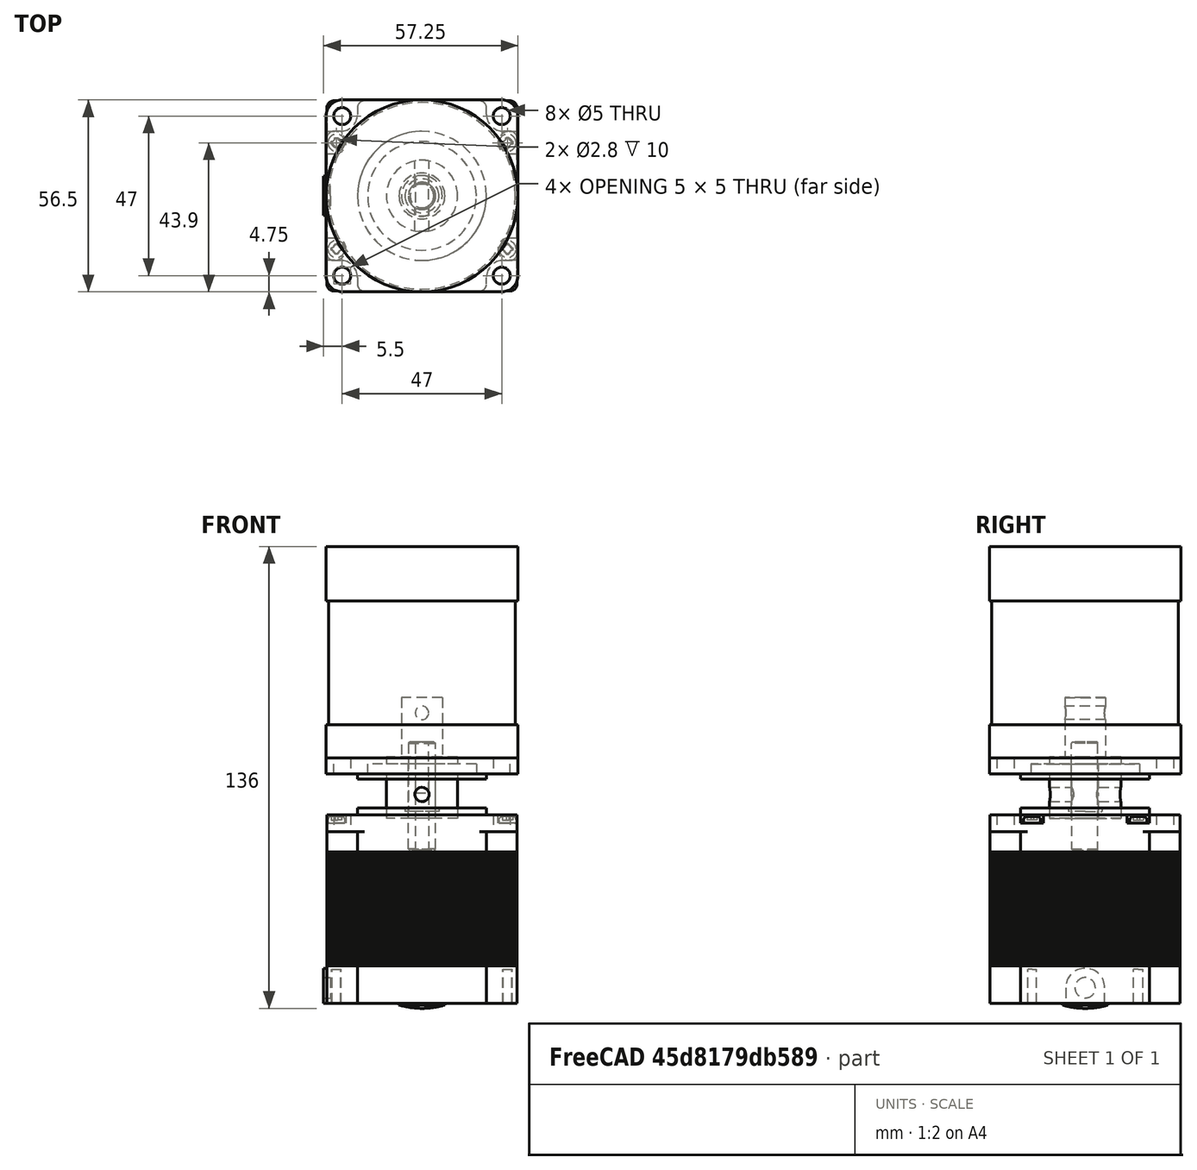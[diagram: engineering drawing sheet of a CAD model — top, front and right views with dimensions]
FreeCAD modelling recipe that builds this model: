
FCSTD DOCUMENT  (FreeCAD 0.20R29410 (Git))
Label: 57BLY-0730NBB
License: All rights reserved
LicenseURL: http://en.wikipedia.org/wiki/All_rights_reserved
objects: TechDraw::DrawViewDimension×11, PartDesign::CoordinateSystem×10, Sketcher::SketchObject×9, TechDraw::DrawProjGroupItem×4, PartDesign::Mirrored×3, PartDesign::Body×3, App::DocumentObjectGroup×3, PartDesign::Pad×2, PartDesign::Revolution×2, App::Link×2, App::Part×2, PartDesign::MultiTransform×1, PartDesign::Groove×1, PartDesign::Hole×1, Part::Feature×1, TechDraw::DrawSVGTemplate×1, App::FeaturePython×1, PartDesign::Pocket×1, TechDraw::DrawProjGroup×1, TechDraw::DrawViewSection×1, +1 more types
note: 41 computed .brp shape members not serialized (recipe doc carries the construction recipe); baked Part::Feature solids carry a one-line shape summary decoded from their .brp

FEATURE [Sketcher::SketchObject] Sketch
  FullyConstrained = true
  MapMode = 5
  Support = -> [XY_Plane]
  sketch-geometry (9):
    g0: LineSegment StartX=0 StartY=0 StartZ=0 EndX=28.25 EndY=0 EndZ=0
    g1: LineSegment StartX=28.25 StartY=0 StartZ=0 EndX=28.25 EndY=23.5386 EndZ=0
    g2: LineSegment StartX=23.5386 StartY=28.25 StartZ=0 EndX=0 EndY=28.25 EndZ=0
    g3: LineSegment StartX=0 StartY=28.25 StartZ=0 EndX=0 EndY=0 EndZ=0
    g4: ArcOfCircle CenterX=23.5386 CenterY=23.5386 CenterZ=0 NormalX=0 NormalY=0 NormalZ=1 AngleXU=0 Radius=4.71142 StartAngle=0 EndAngle=1.5708
    g5: GeomPoint X=28.25 Y=28.25 Z=0
    g6: Circle CenterX=23.5 CenterY=23.5 CenterZ=0 NormalX=0 NormalY=0 NormalZ=1 AngleXU=0 Radius=2.5
    g7: LineSegment StartX=0 StartY=0 StartZ=0 EndX=28.25 EndY=28.25 EndZ=0
    g8: GeomPoint X=26.8701 Y=26.8701 Z=0
  constraints (22):
    c: Coincident(g0,g1)
    c: Coincident(g2,g3)
    c: Coincident(g3,g0)
    c: Horizontal(g0)
    c: Horizontal(g2)
    c: Vertical(g1)
    c: Vertical(g3)
    c: Coincident(g0,g-1)
    c: Equal(g0,g3)
    c: PointOnObject(g5,g2)
    c: PointOnObject(g5,g1)
    c: Tangent(g2,g4) = -1.5708
    c: Tangent(g1,g4) = -1.5708
    c: Coincident(g7,g0)
    c: Coincident(g7,g5)
    c: PointOnObject(g6,g7)
    c: DistanceX(g6) = 23.5
    c: PointOnObject(g8,g4)
    c: PointOnObject(g8,g7)
    c: Distance(g0,g8) = 38
    c: DistanceX(g0) = 28.25  'width'
    c: Diameter(g6) = 5
FEATURE [PartDesign::Pad] Pad
  Direction = (0,0,1)
  Length = 4.7
  Length2 = 10
  Profile = -> Sketch
  ReferenceAxis = -> Sketch [N_Axis]
  Type = 0
FEATURE [PartDesign::Mirrored] Mirrored
  MirrorPlane = -> Sketch [V_Axis]
FEATURE [PartDesign::Mirrored] Mirrored001
  MirrorPlane = -> Sketch [H_Axis]
FEATURE [PartDesign::MultiTransform] MultiTransform
  BaseFeature = -> Pad
  Originals = -> [Pad]
  Transformations = -> [Mirrored,Mirrored001]
FEATURE [Sketcher::SketchObject] Sketch001
  FullyConstrained = true
  MapMode = 5
  Placement = pos=(0,0,0) rot=(1,0,0;1.5708rad)
  Support = -> [XZ_Plane]
  sketch-geometry (10):
    g0: LineSegment StartX=19 StartY=0 StartZ=0 EndX=28.25 EndY=0 EndZ=0
    g1: LineSegment StartX=28.25 StartY=0 StartZ=0 EndX=28.25 EndY=14.5 EndZ=0
    g2: LineSegment StartX=28.25 StartY=14.5 StartZ=0 EndX=27.5 EndY=14.5 EndZ=0
    g3: LineSegment StartX=27.5 StartY=14.5 StartZ=0 EndX=27.5 EndY=51 EndZ=0
    g4: LineSegment StartX=27.5 StartY=51 StartZ=0 EndX=28.25 EndY=51 EndZ=0
    g5: LineSegment StartX=28.25 StartY=51 StartZ=0 EndX=28.25 EndY=67 EndZ=0
    g6: LineSegment StartX=28.25 StartY=67 StartZ=0 EndX=0 EndY=67 EndZ=0
    g7: LineSegment StartX=0 StartY=67 StartZ=0 EndX=0 EndY=-1.5 EndZ=0
    g8: LineSegment StartX=19 StartY=0 StartZ=0 EndX=19 EndY=-1.5 EndZ=0
    g9: LineSegment StartX=19 StartY=-1.5 StartZ=0 EndX=0 EndY=-1.5 EndZ=0
  constraints (31):
    c: PointOnObject(g0,g-1)
    c: Coincident(g0,g1)
    c: Vertical(g1)
    c: Coincident(g1,g2)
    c: Horizontal(g2)
    c: Coincident(g2,g3)
    c: Vertical(g3)
    c: Coincident(g3,g4)
    c: Horizontal(g4)
    c: Coincident(g4,g5)
    c: Vertical(g5)
    c: Coincident(g5,g6)
    c: PointOnObject(g6,g-2)
    c: Horizontal(g6)
    c: Coincident(g6,g7)
    c: Distance(g1) = 14.5
    c: DistanceX(g2) = 27.5
    c: Distance(g3) = 36.5
    c: Vertical(g4,g1)
    c: Distance(g5) = 16
    c: Distance(g7) = 68.5  'total_height'
    c: Vertical(g8)
    c: Coincident(g9,g8)
    c: Horizontal(g9)
    c: DistanceX(g0) = 28.25
    c: Coincident(g0,g8)
    c: Distance(g9) = 19
    c: PointOnObject(g9,g-2)
    c: Coincident(g7,g9)
    c: DistanceY(g7,g-1) = 1.5  'bearing_height'
    c: Horizontal(g0)
FEATURE [PartDesign::Revolution] Revolution
  Angle = 360
  Axis = (0,-2e-16,1)
  Base = (0,0,0)
  BaseFeature = -> MultiTransform
  Profile = -> Sketch001
  ReferenceAxis = -> Sketch001 [V_Axis]
  Reversed = true
FEATURE [PartDesign::Body] Body
  Group = -> [Sketch,Pad,MultiTransform,Mirrored,Mirrored001,Sketch001,Revolution]
  Origin = -> Origin
  Tip = -> Revolution
FEATURE [Sketcher::SketchObject] Sketch002
  FullyConstrained = true
  MapMode = 5
  Support = -> [XY_Plane002]
  expr: .AttachmentOffset.Base.z = 0
  sketch-geometry (3):
    g0: LineSegment StartX=0 StartY=3.5 StartZ=0 EndX=1.93649 EndY=3.5 EndZ=0
    g1: ArcOfCircle CenterX=0 CenterY=0 CenterZ=0 NormalX=0 NormalY=0 NormalZ=1 AngleXU=0 Radius=4 StartAngle=4.71239 EndAngle=7.34862
    g2: LineSegment StartX=-7e-16 StartY=-4 StartZ=0 EndX=0 EndY=3.5 EndZ=0
  constraints (9):
    c: PointOnObject(g0,g-2)
    c: Horizontal(g0)
    c: Coincident(g1,g-1)
    c: PointOnObject(g1,g-2)
    c: Coincident(g1,g0)
    c: Coincident(g2,g1)
    c: Coincident(g2,g0)
    c: Distance(g2) = 7.5
    c: Diameter(g1) = 8
FEATURE [PartDesign::Pad] Pad001
  Direction = (0,0,1)
  Length = 21
  Length2 = 10
  Profile = -> Sketch002
  ReferenceAxis = -> Sketch002 [N_Axis]
  Reversed = true
  Type = 0
FEATURE [PartDesign::Mirrored] Mirrored002
  BaseFeature = -> Pad001
  MirrorPlane = -> Sketch002 [V_Axis]
  Originals = -> [Pad001]
FEATURE [Sketcher::SketchObject] Sketch003
  FullyConstrained = true
  MapMode = 5
  Placement = pos=(0,0,0) rot=(0.57735,0.57735,0.57735;2.0944rad)
  Support = -> [YZ_Plane002]
  expr: Constraints[8] = -Pad001.Length
  sketch-geometry (3):
    g0: LineSegment StartX=3.5 StartY=-21 StartZ=0 EndX=4 EndY=-20.5 EndZ=0
    g1: LineSegment StartX=4 StartY=-20.5 StartZ=0 EndX=4 EndY=-21 EndZ=0
    g2: LineSegment StartX=4 StartY=-21 StartZ=0 EndX=3.5 EndY=-21 EndZ=0
  constraints (9):
    c: Coincident(g0,g1)
    c: Vertical(g1)
    c: Coincident(g1,g2)
    c: Coincident(g2,g0)
    c: Horizontal(g2)
    c: DistanceX(g0) = 3.5
    c: DistanceX(g0) = 4
    c: Equal(g2,g1)
    c: DistanceY(g1) = -21
FEATURE [PartDesign::Groove] Groove
  Angle = 360
  Axis = (-2e-16,3e-16,1)
  Base = (0,0,0)
  BaseFeature = -> Mirrored002
  Profile = -> Sketch003
  ReferenceAxis = -> Sketch003 [V_Axis]
FEATURE [PartDesign::Body] Body001  label="axis"
  Group = -> [Sketch002,Pad001,Mirrored002,Sketch003,Groove]
  Origin = -> Origin002
  Placement = pos=(0,0,-1.5) rot=(0,0,1;0rad)
  Tip = -> Groove
  expr: .Placement.Base.z = -Sketch001.Constraints.bearing_height
FEATURE [PartDesign::CoordinateSystem] fix_center
  AttacherType = Attacher::AttachEngine3D
  MapMode = 2
  Support = -> [XY_Plane001]
FEATURE [PartDesign::CoordinateSystem] LCS_0  label="end"
  AttacherType = Attacher::AttachEngine3D
  AttachmentOffset = pos=(0,0,-13) rot=(0.707107,-0.707107,0;3.14159rad)
  MapMode = 5
  Placement = pos=(0,0,-13) rot=(0.707107,-0.707107,0;3.14159rad)
  Support = -> [XY_Plane003]
  expr: .AttachmentOffset.Base.z = -Sketch005.Constraints.axis_fuxture_cyl_length
FEATURE [Sketcher::SketchObject] Sketch005
  FullyConstrained = true
  MapMode = 5
  Placement = pos=(0,0,0) rot=(1,0,0;1.5708rad)
  Support = -> [XZ_Plane003]
  sketch-geometry (12):
    g0: LineSegment StartX=0 StartY=22.5 StartZ=0 EndX=6 EndY=22.5 EndZ=0
    g1: LineSegment StartX=6 StartY=22.5 StartZ=0 EndX=6 EndY=5 EndZ=0
    g2: LineSegment StartX=6 StartY=5 StartZ=0 EndX=10.5 EndY=5 EndZ=0
    g3: LineSegment StartX=10.5 StartY=5 StartZ=0 EndX=10.5 EndY=3 EndZ=0
    g4: LineSegment StartX=10.5 StartY=3 StartZ=0 EndX=16 EndY=3 EndZ=0
    g5: LineSegment StartX=16 StartY=3 StartZ=0 EndX=16 EndY=0 EndZ=0
    g6: LineSegment StartX=16 StartY=0 StartZ=0 EndX=10.5 EndY=0 EndZ=0
    g7: LineSegment StartX=10.5 StartY=0 StartZ=0 EndX=10.5 EndY=-13 EndZ=0
    g8: LineSegment StartX=10.5 StartY=-13 StartZ=0 EndX=4 EndY=-13 EndZ=0
    g9: LineSegment StartX=4 StartY=-13 StartZ=0 EndX=4 EndY=3 EndZ=0
    g10: LineSegment StartX=4 StartY=3 StartZ=0 EndX=0 EndY=3 EndZ=0
    g11: LineSegment StartX=0 StartY=3 StartZ=0 EndX=0 EndY=22.5 EndZ=0
  constraints (37):
    c: Horizontal(g0)
    c: Coincident(g0,g1)
    c: Vertical(g1)
    c: Coincident(g1,g2)
    c: Horizontal(g2)
    c: Coincident(g2,g3)
    c: Vertical(g3)
    c: Coincident(g3,g4)
    c: Coincident(g4,g5)
    c: Vertical(g5)
    c: Coincident(g5,g6)
    c: Horizontal(g6)
    c: Coincident(g6,g7)
    c: Vertical(g7)
    c: Coincident(g7,g8)
    c: Horizontal(g8)
    c: Coincident(g8,g9)
    c: Vertical(g9)
    c: Horizontal(g4)
    c: DistanceX(g0) = 6
    c: DistanceX(g2) = 10.5
    c: DistanceX(g4) = 16
    c: DistanceX(g7) = 10.5
    c: DistanceX(g8) = 4
    c: DistanceY(g3,g3) = 2
    c: DistanceY(g3,g0) = 19.5
    c: DistanceY(g5,g5) = 3  'shield_length'
    c: Distance(g7,g6) = 13  'axis_fuxture_cyl_length'
    c: Horizontal(g-1,g6)
    c: DistanceY(g0) = 22.5  'shield_to_end'
    c: PointOnObject(g10,g-2)
    c: Horizontal(g10)
    c: Coincident(g11,g10)
    c: Vertical(g11)
    c: DistanceY(g8,g10) = 16  'axis_length'
    c: Coincident(g9,g10)
    c: Coincident(g11,g0)
FEATURE [PartDesign::Revolution] Revolution001
  Angle = 360
  Axis = (0,-2e-16,1)
  Base = (0,0,0)
  Placement = pos=(0,0,0) rot=(1,0,0;1.5708rad)
  Profile = -> Sketch005
  ReferenceAxis = -> Sketch005 [V_Axis]
  Reversed = true
FEATURE [Sketcher::SketchObject] Sketch006
  AttachmentOffset = pos=(0,-6,20) rot=(0,0,1;0rad)
  FullyConstrained = true
  MapMode = 5
  Placement = pos=(0,-20,-6) rot=(1,0,0;1.5708rad)
  Support = -> [XZ_Plane003]
  expr: .AttachmentOffset.Base.y = -Sketch005.Constraints.axis_fuxture_cyl_length + 7mm
  sketch-geometry (1):
    g0: Circle CenterX=0 CenterY=0 CenterZ=0 NormalX=0 NormalY=0 NormalZ=1 AngleXU=0 Radius=2
  constraints (2):
    c: Coincident(g0,g-1)
    c: Diameter(g0) = 4
FEATURE [PartDesign::Hole] Hole
  BaseFeature = -> Revolution001
  CustomThreadClearance = 0
  Depth = 117.943
  DepthType = 1
  Diameter = 4.2
  DrillForDepth = false
  DrillPoint = 1
  DrillPointAngle = 117
  HoleCutCountersinkAngle = 90
  HoleCutCustomValues = false
  HoleCutDepth = 0
  HoleCutDiameter = 6.1
  HoleCutType = 0
  ModelThread = false
  Placement = pos=(0,0,0) rot=(1,0,0;1.5708rad)
  Profile = -> Sketch006
  Tapered = true
  TaperedAngle = 90
  ThreadClass = 0
  ThreadDepth = 117.943
  ThreadDepthType = 0
  ThreadDirection = 0
  ThreadFit = 0
  ThreadSize = 13
  ThreadType = 1
  Threaded = true
  UseCustomThreadClearance = false
FEATURE [Part::Feature] Part__Feature  label="57HS56-2804A08-D21"
  Placement = pos=(0,0,-17) rot=(0,-1,0;1.5708rad)
  shape: bbox 57 x 56 x 78.5 mm, 1908 faces, 69 solids (baked)
FEATURE [Sketcher::SketchObject] Sketch010
  FullyConstrained = false
  MapMode = 5
  Placement = pos=(0,0,0) rot=(1,0,0;1.5708rad)
  Support = -> [XZ_Plane003]
  sketch-geometry (6):
    g0: LineSegment StartX=9.5 StartY=-0.0613249 StartZ=0 EndX=9.5 EndY=0 EndZ=0
    g1: LineSegment StartX=9.5 StartY=0 StartZ=0 EndX=9.5 EndY=0.0613249 EndZ=0
    g2: LineSegment StartX=9.5 StartY=0.0613249 StartZ=0 EndX=10 EndY=0.35 EndZ=0
    g3: LineSegment StartX=10 StartY=0.35 StartZ=0 EndX=10 EndY=0 EndZ=0
    g4: LineSegment StartX=10 StartY=0 StartZ=0 EndX=10 EndY=-0.35 EndZ=0
    g5: LineSegment StartX=10 StartY=-0.35 StartZ=0 EndX=9.5 EndY=-0.0613249 EndZ=0
  constraints (17):
    c: PointOnObject(g0,g-1)
    c: Vertical(g0)
    c: Coincident(g0,g1)
    c: Vertical(g1)
    c: Coincident(g1,g2)
    c: Coincident(g2,g3)
    c: PointOnObject(g3,g-1)
    c: Vertical(g3)
    c: Coincident(g3,g4)
    c: Vertical(g4)
    c: Coincident(g4,g5)
    c: Coincident(g5,g0)
    c: Equal(g0,g1)
    c: Equal(g4,g3)
    c: DistanceX(g3) = 10
    c: DistanceX(g0,g3) = 0.5
    c: Angle(g-1,g5) = 2.61799
FEATURE [Sketcher::SketchObject] Sketch011
  FullyConstrained = true
  MapMode = 5
  Support = -> [XY_Plane003]
  sketch-geometry (1):
    g0: Circle CenterX=0 CenterY=0 CenterZ=0 NormalX=0 NormalY=0 NormalZ=1 AngleXU=0 Radius=10
  constraints (2):
    c: Coincident(g0,g-1)
    c: Diameter(g0) = 20
FEATURE [TechDraw::DrawSVGTemplate] Template
  EditableTexts = Designed_by_Name=Designed by Name; Drawing_number=Drawing number; FC-Date=Date; FC-SC=Scale; FC-SH=Sheet; FC-Title=Title; Subtitle=Subtitle; Weight=Weight
  Height = 210
  Orientation = 1
  Width = 297
FEATURE [PartDesign::CoordinateSystem] LCS_Origin
  AttacherType = Attacher::AttachEngine3D
  MapMode = 2
  Support = -> [X_Axis005]
FEATURE [App::DocumentObjectGroup] Constraints
FEATURE [App::FeaturePython] Variables  # WARN: FeaturePython — macro-defined, semantics opaque (R4)
  Type = App::PropertyContainer
FEATURE [App::DocumentObjectGroup] Configurations
FEATURE [App::Link] _7BLY_0730NBB  label="57BLY-0730NBB001"
  AssemblyType = Part::Link
  AttachedBy = #fix_center
  AttachedTo = Parent Assembly#LCS_Origin
  LinkedObject = -> Part
  SolverId = Asm4EE
  expr: Placement = LCS_Origin.Placement * AttachmentOffset * fix_center.Placement ^ -1
FEATURE [PartDesign::CoordinateSystem] fixture_plane
  AttacherType = Attacher::AttachEngine3D
  AttachmentOffset = pos=(0,0,0) rot=(1,0,0;3.14159rad)
  MapMode = 5
  Placement = pos=(0,0,0) rot=(1,0,0;3.14159rad)
  Support = -> [XY_Plane001]
FEATURE [PartDesign::CoordinateSystem] axis_root
  AttacherType = Attacher::AttachEngine3D
  AttachmentOffset = pos=(0,0,-1.5) rot=(1,0,0;3.14159rad)
  MapMode = 5
  Placement = pos=(0,0,-1.5) rot=(1,0,0;3.14159rad)
  Support = -> [XY_Plane001]
  expr: .AttachmentOffset.Base.z = -Sketch001.Constraints.bearing_height
FEATURE [PartDesign::CoordinateSystem] axis_end
  AttacherType = Attacher::AttachEngine3D
  AttachmentOffset = pos=(0,0,21) rot=(0,0,1;0rad)
  MapMode = 2
  Placement = pos=(0,-2.6e-15,-22.5) rot=(1,0,0;3.14159rad)
  Support = -> [axis_root]
  expr: .AttachmentOffset.Base.z = Pad001.Length
FEATURE [App::Part] Part  label="57BLY-0730NBB"
  Group = -> [Body,Body001,fix_center,fixture_plane,axis_root,axis_end]
  Origin = -> Origin001
FEATURE [PartDesign::CoordinateSystem] Local_CS
  AttacherType = Attacher::AttachEngine3D
  AttachmentOffset = pos=(0,0,3) rot=(0,0,1;0rad)
  MapMode = 5
  Placement = pos=(0,0,3) rot=(0,0,1;0rad)
  Support = -> [XY_Plane003]
  expr: .AttachmentOffset.Base.z = Sketch005.Constraints.axis_length - Sketch005.Constraints.axis_fuxture_cyl_length
FEATURE [App::Link] cap001
  AssemblyType = Part::Link
  AttachedBy = #Local_CS
  AttachedTo = _7BLY_0730NBB#axis_end
  LinkPlacement = pos=(0,-2.2e-15,-19.5) rot=(1,0,0;3.14159rad)
  LinkedObject = -> cap
  Placement = pos=(0,-2.2e-15,-19.5) rot=(1,0,0;3.14159rad)
  SolverId = Asm4EE
  expr: Placement = _7BLY_0730NBB.Placement * axis_end.Placement * AttachmentOffset * Local_CS.Placement ^ -1
FEATURE [PartDesign::CoordinateSystem] fixture_plane001
  AttacherType = Attacher::AttachEngine3D
  MapMode = 5
  Placement = pos=(0,0,0) rot=(1,0,0;3.14159rad)
  Support = -> [fixture_plane]
FEATURE [PartDesign::CoordinateSystem] disk_fixture
  AttacherType = Attacher::AttachEngine3D
  AttachmentOffset = pos=(0,0,3) rot=(0,0,1;0rad)
  MapMode = 5
  Placement = pos=(0,0,3) rot=(0,0,1;0rad)
  Support = -> [XY_Plane003]
  expr: .AttachmentOffset.Base.z = Sketch005.Constraints.shield_length
FEATURE [PartDesign::CoordinateSystem] LCS_1
  AttacherType = Attacher::AttachEngine3D
  AttachmentOffset = pos=(0,-2.9e-15,-25.5) rot=(1,0,0;3.14159rad)
  MapMode = 5
  Placement = pos=(0,-2.9e-15,-22.5) rot=(1,0,0;3.14159rad)
  Support = -> [disk_fixture]
  expr: AttachmentOffset = cap001.Placement * disk_fixture.Placement * disk_fixture.Placement
FEATURE [App::Part] Model
  AssemblyType = Part::Link
  Group = -> [LCS_Origin,Constraints,Variables,Configurations,_7BLY_0730NBB,cap001,fixture_plane001,LCS_1]
  Origin = -> Origin005
  Type = Assembly
FEATURE [Sketcher::SketchObject] Sketch012
  FullyConstrained = true
  MapMode = 5
  Placement = pos=(0,0,0) rot=(1,0,0;1.5708rad)
  Support = -> [XZ_Plane003]
  expr: .Constraints.axis_fuxture_cyl_length = Sketch005.Constraints.axis_fuxture_cyl_length
  expr: .Constraints.shield_length = Sketch005.Constraints.shield_length
  expr: Constraints[22] = Sketch005.Constraints[19]
  expr: Constraints[23] = Sketch005.Constraints[20]
  expr: Constraints[24] = Sketch005.Constraints[21]
  expr: Constraints[25] = Sketch005.Constraints[22]
  expr: Constraints[26] = Sketch005.Constraints[23]
  expr: Constraints[27] = Sketch005.Constraints[24]
  expr: Constraints[28] = Sketch005.Constraints[25]
  sketch-geometry (12):
    g0: Circle CenterX=0 CenterY=18 CenterZ=0 NormalX=0 NormalY=0 NormalZ=1 AngleXU=0 Radius=2
    g1: LineSegment StartX=4 StartY=22.5 StartZ=0 EndX=6 EndY=22.5 EndZ=0
    g2: LineSegment StartX=6 StartY=22.5 StartZ=0 EndX=6 EndY=5 EndZ=0
    g3: LineSegment StartX=6 StartY=5 StartZ=0 EndX=10.5 EndY=5 EndZ=0
    g4: LineSegment StartX=10.5 StartY=5 StartZ=0 EndX=10.5 EndY=3 EndZ=0
    g5: LineSegment StartX=10.5 StartY=3 StartZ=0 EndX=16 EndY=3 EndZ=0
    g6: LineSegment StartX=16 StartY=3 StartZ=0 EndX=16 EndY=0 EndZ=0
    g7: LineSegment StartX=16 StartY=0 StartZ=0 EndX=10.5 EndY=0 EndZ=0
    g8: LineSegment StartX=10.5 StartY=0 StartZ=0 EndX=10.5 EndY=-13 EndZ=0
    g9: LineSegment StartX=10.5 StartY=-13 StartZ=0 EndX=4 EndY=-13 EndZ=0
    g10: LineSegment StartX=4 StartY=-13 StartZ=0 EndX=4 EndY=22.5 EndZ=0
    g11: GeomPoint X=0 Y=16 Z=0
  constraints (36):
    c: PointOnObject(g0,g-2)
    c: Diameter(g0) = 4
    c: Horizontal(g1)
    c: Coincident(g1,g2)
    c: Vertical(g2)
    c: Coincident(g2,g3)
    c: Horizontal(g3)
    c: Coincident(g3,g4)
    c: Vertical(g4)
    c: Coincident(g4,g5)
    c: Coincident(g5,g6)
    c: Vertical(g6)
    c: Coincident(g6,g7)
    c: Horizontal(g7)
    c: Coincident(g7,g8)
    c: Vertical(g8)
    c: Coincident(g8,g9)
    c: Horizontal(g9)
    c: Coincident(g9,g10)
    c: Vertical(g10)
    c: Coincident(g1,g10)
    c: Horizontal(g5)
    c: DistanceX(g1) = 6
    c: DistanceX(g3) = 10.5
    c: DistanceX(g5) = 16
    c: DistanceX(g8) = 10.5
    c: DistanceX(g9) = 4
    c: DistanceY(g4,g4) = 2
    c: DistanceY(g4,g1) = 19.5
    c: DistanceY(g6,g6) = 3  'shield_length'
    c: Distance(g8,g7) = 13  'axis_fuxture_cyl_length'
    c: Horizontal(g-1,g7)
    c: DistanceY(g1) = 22.5  'shield_to_end'
    c: PointOnObject(g11,g-2)
    c: PointOnObject(g11,g0)
    c: DistanceY(g2,g11) = 11
FEATURE [PartDesign::Pocket] Pocket
  BaseFeature = -> Hole
  Direction = (0,1,2e-16)
  Length = 5
  Length2 = 5
  Midplane = true
  Placement = pos=(0,0,0) rot=(1,0,0;1.5708rad)
  Profile = -> Sketch012
  ReferenceAxis = -> Sketch012 [N_Axis]
  Type = 1
FEATURE [PartDesign::Body] cap
  Group = -> [LCS_0,Sketch005,Revolution001,Sketch006,Hole,Sketch010,Sketch011,Local_CS,disk_fixture,Sketch012,Pocket]
  Origin = -> Origin003
  Tip = -> Pocket
FEATURE [TechDraw::DrawProjGroupItem] ProjItem  label="Front"
  CoarseView = false
  Direction = (0,-1,0)
  Focus = 100
  HardHidden = false
  IsoCount = 0
  IsoHidden = false
  IsoVisible = false
  LockPosition = true
  Perspective = false
  Rotation = 0
  RotationVector = (1,0,0)
  ScaleType = 2
  SeamHidden = false
  SeamVisible = true
  SmoothHidden = false
  SmoothVisible = true
  Source = -> [cap]
  Type = 0
  X = 0
  XDirection = (1,0,0)
  Y = 0
FEATURE [TechDraw::DrawProjGroupItem] ProjItem001  label="Bottom"
  CoarseView = false
  Direction = (0,0,-1)
  Focus = 100
  HardHidden = false
  IsoCount = 0
  IsoHidden = false
  IsoVisible = false
  LockPosition = false
  Perspective = false
  Rotation = 0
  RotationVector = (1,0,0)
  ScaleType = 2
  SeamHidden = false
  SeamVisible = true
  SmoothHidden = false
  SmoothVisible = true
  Source = -> [cap]
  Type = 5
  X = 0
  XDirection = (1,0,0)
  Y = 50.5
FEATURE [TechDraw::DrawProjGroupItem] ProjItem002  label="Top"
  CoarseView = false
  Direction = (0,0,1)
  Focus = 100
  HardHidden = false
  IsoCount = 0
  IsoHidden = false
  IsoVisible = false
  LockPosition = false
  Perspective = false
  Rotation = 0
  RotationVector = (1,0,0)
  ScaleType = 2
  SeamHidden = false
  SeamVisible = true
  SmoothHidden = false
  SmoothVisible = true
  Source = -> [cap]
  Type = 4
  X = 0
  XDirection = (1,0,0)
  Y = -50.5
FEATURE [TechDraw::DrawProjGroupItem] ProjItem003  label="Left"
  CoarseView = false
  Direction = (-1,-1e-16,0)
  Focus = 100
  HardHidden = false
  IsoCount = 0
  IsoHidden = false
  IsoVisible = false
  LockPosition = false
  Perspective = false
  Rotation = 0
  RotationVector = (1,0,0)
  ScaleType = 2
  SeamHidden = false
  SeamVisible = true
  SmoothHidden = false
  SmoothVisible = true
  Source = -> [cap]
  Type = 1
  X = 47
  XDirection = (1e-16,-1,0)
  Y = 0
FEATURE [TechDraw::DrawProjGroup] ProjGroup
  Anchor = -> ProjItem
  AutoDistribute = true
  LockPosition = false
  ProjectionType = 0
  Rotation = 0
  ScaleType = 0
  Source = -> [cap]
  Views = -> [ProjItem,ProjItem001,ProjItem002,ProjItem003]
  X = 80
  Y = 130
  spacingX = 15
  spacingY = 15
FEATURE [App::DocumentObjectGroup] Parts
  Group = -> [Part,cap]
FEATURE [TechDraw::DrawViewDimension] Dimension
  AngleOverride = false
  Arbitrary = false
  ArbitraryTolerances = false
  EqualTolerance = true
  ExtensionAngle = 0
  FormatSpec = %.2w
  FormatSpecOverTolerance = %+.2w
  FormatSpecUnderTolerance = %+.2w
  Inverted = false
  LineAngle = 0
  LockPosition = false
  MeasureType = 1
  OverTolerance = 0
  References2D = -> [ProjItem003]
  Rotation = 0
  ScaleType = 0
  TheoreticalExact = false
  Type = 2
  UnderTolerance = 0
  X = 28.2563
  Y = 16.3611
FEATURE [TechDraw::DrawViewDimension] Dimension001
  AngleOverride = false
  Arbitrary = false
  ArbitraryTolerances = false
  EqualTolerance = true
  ExtensionAngle = 0
  FormatSpec = %.2w
  FormatSpecOverTolerance = %+.2w
  FormatSpecUnderTolerance = %+.2w
  Inverted = false
  LineAngle = 0
  LockPosition = false
  MeasureType = 1
  OverTolerance = 0
  References2D = -> [ProjItem003]
  Rotation = 0
  ScaleType = 0
  TheoreticalExact = false
  Type = 2
  UnderTolerance = 0
  X = -15.6179
  Y = 10.5677
FEATURE [TechDraw::DrawViewDimension] Dimension002
  AngleOverride = false
  Arbitrary = false
  ArbitraryTolerances = false
  EqualTolerance = true
  ExtensionAngle = 0
  FormatSpec = %.2w
  FormatSpecOverTolerance = %+.2w
  FormatSpecUnderTolerance = %+.2w
  Inverted = false
  LineAngle = 0
  LockPosition = false
  MeasureType = 1
  OverTolerance = 0
  References2D = -> [ProjItem003]
  Rotation = 0
  ScaleType = 0
  TheoreticalExact = false
  Type = 2
  UnderTolerance = 0
  X = -25.1076
  Y = -4.04958
FEATURE [TechDraw::DrawViewDimension] Dimension003
  AngleOverride = false
  Arbitrary = false
  ArbitraryTolerances = false
  EqualTolerance = true
  ExtensionAngle = 0
  FormatSpec = %.2w
  FormatSpecOverTolerance = %+.2w
  FormatSpecUnderTolerance = %+.2w
  Inverted = false
  LineAngle = 0
  LockPosition = false
  MeasureType = 1
  OverTolerance = 0
  References2D = -> [ProjItem003]
  Rotation = 0
  ScaleType = 0
  TheoreticalExact = false
  Type = 2
  UnderTolerance = 0
  X = 26.4789
  Y = -10.5468
FEATURE [TechDraw::DrawViewDimension] Dimension004
  AngleOverride = false
  Arbitrary = false
  ArbitraryTolerances = false
  EqualTolerance = true
  ExtensionAngle = 0
  FormatSpec = %.2w
  FormatSpecOverTolerance = %+.2w
  FormatSpecUnderTolerance = %+.2w
  Inverted = false
  LineAngle = 0
  LockPosition = false
  MeasureType = 1
  OverTolerance = 0
  References2D = -> [ProjItem]
  Rotation = 0
  ScaleType = 0
  TheoreticalExact = false
  Type = 5
  UnderTolerance = 0
  X = 23.5054
  Y = 18.0041
FEATURE [TechDraw::DrawViewDimension] Dimension005
  AngleOverride = false
  Arbitrary = true
  ArbitraryTolerances = false
  EqualTolerance = true
  ExtensionAngle = 0
  FormatSpec = M5
  FormatSpecOverTolerance = %+.2w
  FormatSpecUnderTolerance = %+.2w
  Inverted = false
  LineAngle = 0
  LockPosition = false
  MeasureType = 1
  OverTolerance = 0
  References2D = -> [ProjItem]
  Rotation = 0
  ScaleType = 0
  TheoreticalExact = false
  Type = 5
  UnderTolerance = 0
  X = 14.9531
  Y = -5.91701
FEATURE [TechDraw::DrawViewDimension] Dimension006
  AngleOverride = false
  Arbitrary = false
  ArbitraryTolerances = false
  EqualTolerance = true
  ExtensionAngle = 0
  FormatSpec = %.2w
  FormatSpecOverTolerance = %+.2w
  FormatSpecUnderTolerance = %+.2w
  Inverted = false
  LineAngle = 0
  LockPosition = false
  MeasureType = 1
  OverTolerance = 0
  References2D = -> [ProjItem]
  Rotation = 0
  ScaleType = 0
  TheoreticalExact = false
  Type = 2
  UnderTolerance = 0
  X = -25.4044
  Y = 10.1322
FEATURE [TechDraw::DrawViewDimension] Dimension007
  AngleOverride = false
  Arbitrary = false
  ArbitraryTolerances = false
  EqualTolerance = true
  ExtensionAngle = 0
  FormatSpec = %.2w
  FormatSpecOverTolerance = %+.2w
  FormatSpecUnderTolerance = %+.2w
  Inverted = false
  LineAngle = 0
  LockPosition = false
  MeasureType = 1
  OverTolerance = 0
  References2D = -> [ProjItem]
  Rotation = 0
  ScaleType = 0
  TheoreticalExact = false
  Type = 2
  UnderTolerance = 0
  X = -28.0992
  Y = -10.4709
FEATURE [TechDraw::DrawViewDimension] Dimension008
  AngleOverride = false
  Arbitrary = true
  ArbitraryTolerances = false
  EqualTolerance = true
  ExtensionAngle = 0
  FormatSpec = M12
  FormatSpecOverTolerance = %+.2w
  FormatSpecUnderTolerance = %+.2w
  Inverted = false
  LineAngle = 0
  LockPosition = false
  MeasureType = 1
  OverTolerance = 0
  References2D = -> [ProjItem]
  Rotation = 0
  ScaleType = 0
  TheoreticalExact = false
  Type = 1
  UnderTolerance = 0
  X = -0.041045
  Y = 25.8866
FEATURE [TechDraw::DrawViewSection] SectionView  label="Section  - "
  BaseView = -> ProjItem001
  CoarseView = false
  CutSurfaceDisplay = 2
  Direction = (0,-1,0)
  FileGeomPattern = <path>
  FileHatchPattern = <path>
  Focus = 100
  FuseBeforeCut = false
  HardHidden = false
  HatchScale = 1
  IsoCount = 0
  IsoHidden = false
  IsoVisible = false
  LockPosition = false
  NameGeomPattern = Diamond
  Perspective = false
  Rotation = 0
  ScaleType = 2
  SeamHidden = false
  SeamVisible = true
  SectionDirection = 3
  SectionNormal = (0,-1,0)
  SectionOrigin = (0.04,0,4.74)
  SmoothHidden = false
  SmoothVisible = true
  Source = -> [cap]
  X = 184
  XDirection = (1,0,0)
  Y = 130
FEATURE [TechDraw::DrawViewDimension] Dimension009
  AngleOverride = false
  Arbitrary = false
  ArbitraryTolerances = false
  EqualTolerance = true
  ExtensionAngle = 0
  FormatSpec = %.2w
  FormatSpecOverTolerance = %+.2w
  FormatSpecUnderTolerance = %+.2w
  Inverted = false
  LineAngle = 0
  LockPosition = false
  MeasureType = 1
  OverTolerance = 0
  References2D = -> [SectionView]
  Rotation = 0
  ScaleType = 0
  TheoreticalExact = false
  Type = 2
  UnderTolerance = 0
  X = 38.487
  Y = -5
FEATURE [TechDraw::DrawViewDimension] Dimension010
  AngleOverride = false
  Arbitrary = false
  ArbitraryTolerances = false
  EqualTolerance = true
  ExtensionAngle = 0
  FormatSpec = %.2w
  FormatSpecOverTolerance = %+.2w
  FormatSpecUnderTolerance = %+.2w
  Inverted = false
  LineAngle = 0
  LockPosition = false
  MeasureType = 1
  OverTolerance = 0
  References2D = -> [SectionView]
  Rotation = 0
  ScaleType = 0
  TheoreticalExact = false
  Type = 1
  UnderTolerance = 0
  X = 8.96038
  Y = -30
FEATURE [TechDraw::DrawPage] Page
  KeepUpdated = false
  NextBalloonIndex = 3
  ProjectionType = 0
  Template = -> Template
  Views = -> [ProjGroup,Dimension,Dimension001,Dimension002,Dimension003,Dimension004,Dimension005,Dimension006,Dimension007,Dimension008,SectionView,Dimension009,Dimension010]
note: 2 file-system paths scrubbed to <path> (originals preserved in the JSON sidecar)
